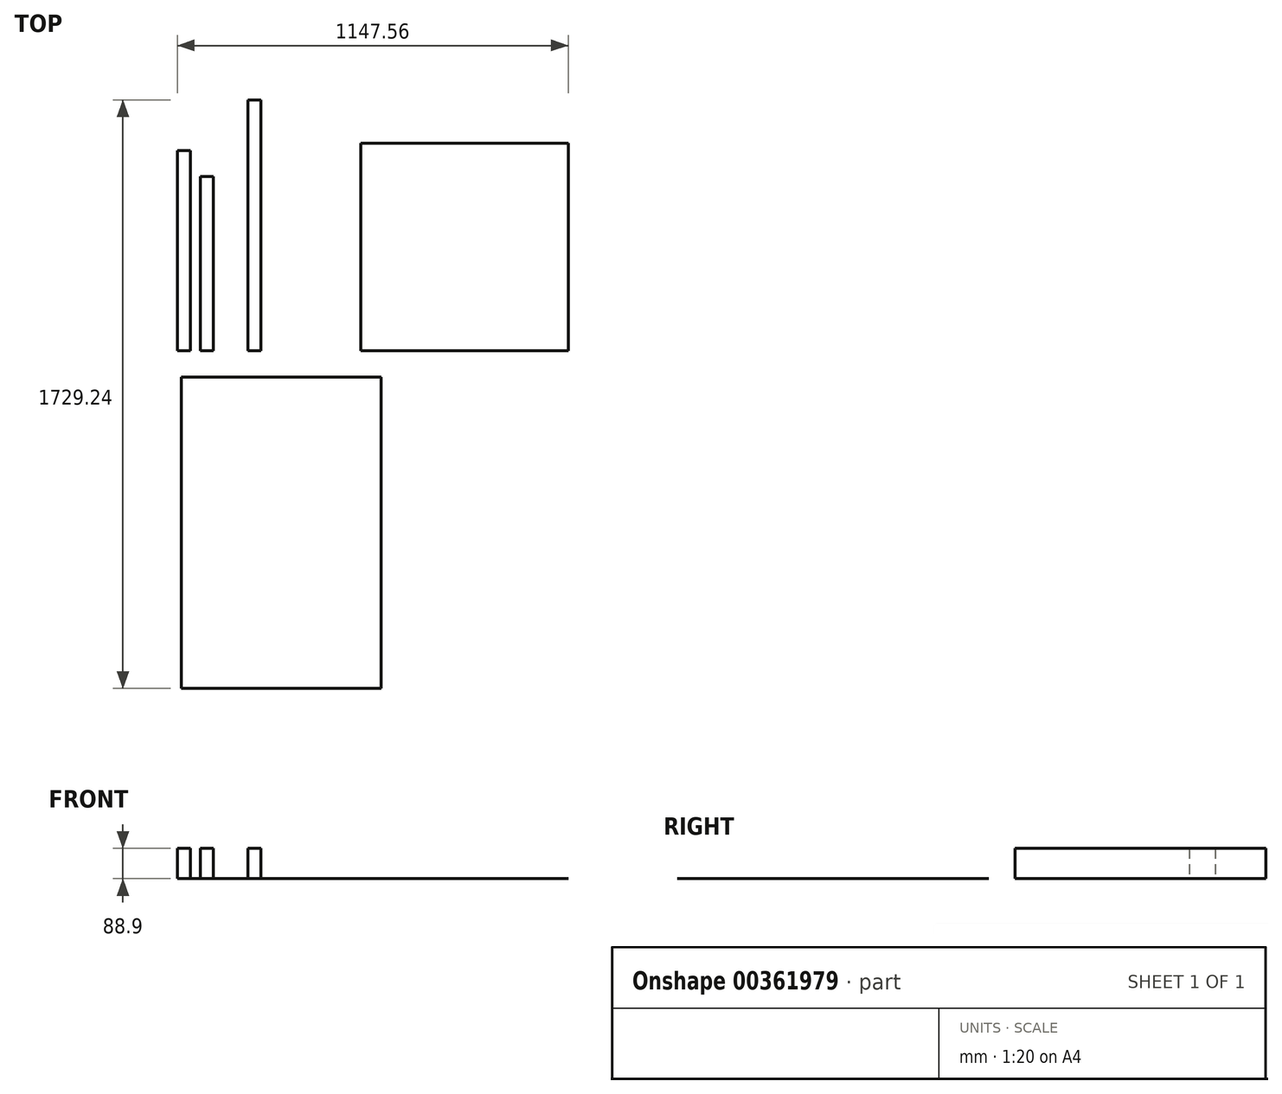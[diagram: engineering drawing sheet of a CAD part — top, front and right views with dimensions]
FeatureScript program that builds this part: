
annotation { "Feature Type Name" : "Feature", "Feature Type Description" : "" }
export const myFeature = defineFeature(function(context is Context, id is Id, definition is map)
    precondition{}
    {
        {
            var Q0;
            Q0=qCreatedBy(makeId("Top.planeOp"),FACE);
            var sketch = newSketch(context, id + "F0", { "sketchPlane" : qUnion([Q0])});
            skLineSegment(sketch, "E0.bottom", {"start": v(0, 0) * mm, "end": v(38.1, 0) * mm});
            skLineSegment(sketch, "E0.top", {"start": v(0, 587.38) * mm, "end": v(38.1, 587.38) * mm});
            skLineSegment(sketch, "E0.left", {"start": v(0, 0) * mm, "end": v(0, 587.38) * mm});
            skLineSegment(sketch, "E0.right", {"start": v(38.1, 0) * mm, "end": v(38.1, 587.38) * mm});
            skSolve(sketch);
        }
        {
            var Q0;
            Q0 = qSketchRegion(id + "F0", true);
            extrude(context, id + "F1", {"entities" : qUnion([Q0]), "depth" : 88.9 * mm});
        }
        {
            var Q0;
            Q0=qCreatedBy(makeId("Top.planeOp"),FACE);
            var sketch = newSketch(context, id + "F2", { "sketchPlane" : qUnion([Q0])});
            skLineSegment(sketch, "E1.bottom", {"start": v(206.97, 0) * mm, "end": v(245.07, 0) * mm});
            skLineSegment(sketch, "E1.top", {"start": v(206.97, 736.6) * mm, "end": v(245.07, 736.6) * mm});
            skLineSegment(sketch, "E1.left", {"start": v(206.97, 0) * mm, "end": v(206.97, 736.6) * mm});
            skLineSegment(sketch, "E1.right", {"start": v(245.07, 0) * mm, "end": v(245.07, 736.6) * mm});
            skSolve(sketch);
        }
        {
            var Q0;
            Q0=makeQuery(id+"F2.imprint","IMPRINT",FACE,{"disambiguationData":[TD([[makeQuery(id+"F2.imprint","IMPRINT",EDGE,{"derivedFrom":sQuery(id+"F2.wireOp",EDGE,"E1.bottom")}),1.0]])]});
            extrude(context, id + "F3", {"entities" : qUnion([Q0]), "depth" : 88.9 * mm});
        }
        {
            var Q0;
            Q0=qCreatedBy(makeId("Top.planeOp"),FACE);
            var sketch = newSketch(context, id + "F4", { "sketchPlane" : qUnion([Q0])});
            skLineSegment(sketch, "E2.bottom", {"start": v(67.44, 0) * mm, "end": v(105.54, 0) * mm});
            skLineSegment(sketch, "E2.top", {"start": v(67.44, 511.18) * mm, "end": v(105.54, 511.18) * mm});
            skLineSegment(sketch, "E2.left", {"start": v(67.44, 0) * mm, "end": v(67.44, 511.17) * mm});
            skLineSegment(sketch, "E2.right", {"start": v(105.54, 0) * mm, "end": v(105.54, 511.17) * mm});
            skSolve(sketch);
        }
        {
            var Q0;
            Q0=makeQuery(id+"F4.imprint","IMPRINT",FACE,{"disambiguationData":[TD([[makeQuery(id+"F4.imprint","IMPRINT",EDGE,{"derivedFrom":sQuery(id+"F4.wireOp",EDGE,"E2.bottom")}),1.0]])]});
            extrude(context, id + "F5", {"entities" : qUnion([Q0]), "depth" : 88.9 * mm});
        }
        {
            var Q0;
            Q0=qCreatedBy(makeId("Top.planeOp"),FACE);
            var sketch = newSketch(context, id + "F6", { "sketchPlane" : qUnion([Q0])});
            skLineSegment(sketch, "E3.bottom", {"start": v(537.96, 0) * mm, "end": v(1147.56, 0) * mm});
            skLineSegment(sketch, "E3.top", {"start": v(537.96, 609.6) * mm, "end": v(1147.56, 609.6) * mm});
            skLineSegment(sketch, "E3.left", {"start": v(537.96, 0) * mm, "end": v(537.96, 609.6) * mm});
            skLineSegment(sketch, "E3.right", {"start": v(1147.56, 0) * mm, "end": v(1147.56, 609.6) * mm});
            skSolve(sketch);
        }
        {
            var Q0;
            Q0=makeQuery(id+"F6.imprint","IMPRINT",FACE,{"disambiguationData":[TD([[makeQuery(id+"F6.imprint","IMPRINT",EDGE,{"derivedFrom":sQuery(id+"F6.wireOp",EDGE,"E3.bottom")}),1.0]])]});
            extrude(context, id + "F7", {"entities" : qUnion([Q0]), "depth" : 3 / 101.6 * mm});
        }
        {
            var Q0;
            Q0=qCreatedBy(makeId("Top.planeOp"),FACE);
            var sketch = newSketch(context, id + "F8", { "sketchPlane" : qUnion([Q0])});
            skLineSegment(sketch, "E4.bottom", {"start": v(0, -78.24) * mm, "end": v(609.6, -78.24) * mm});
            skLineSegment(sketch, "E4.top", {"start": v(0, -992.64) * mm, "end": v(609.6, -992.64) * mm});
            skLineSegment(sketch, "E4.left", {"start": v(0, -78.24) * mm, "end": v(0, -992.64) * mm});
            skLineSegment(sketch, "E4.right", {"start": v(609.6, -78.24) * mm, "end": v(609.6, -992.64) * mm});
            skSolve(sketch);
        }
        {
            var Q0;
            Q0=makeQuery(id+"F8.imprint","IMPRINT",FACE,{"disambiguationData":[TD([[makeQuery(id+"F8.imprint","IMPRINT",EDGE,{"derivedFrom":sQuery(id+"F8.wireOp",EDGE,"E4.bottom")}),-1.0]])]});
            extrude(context, id + "F9", {"entities" : qUnion([Q0]), "depth" : 7 / 406.4 * mm});
        }
        {
            var Q0;
            Q0=makeQuery(id+"F9.opExtrude","CAP_EDGE",EDGE,{"disambiguationData":[OSD([sQuery(id+"F8.wireOp",EDGE,"E4.right")])],"isStart":false});
            var Q1;
            Q1=makeQuery(id+"F9.opExtrude","CAP_EDGE",EDGE,{"disambiguationData":[OSD([sQuery(id+"F8.wireOp",EDGE,"E4.left")])],"isStart":false});
            chamfer(context, id + "F10", {"entities" : qUnion([Q0, Q1]), "width" : 11.18 * mm, "tangentPropagation" : true});
        }
    });
